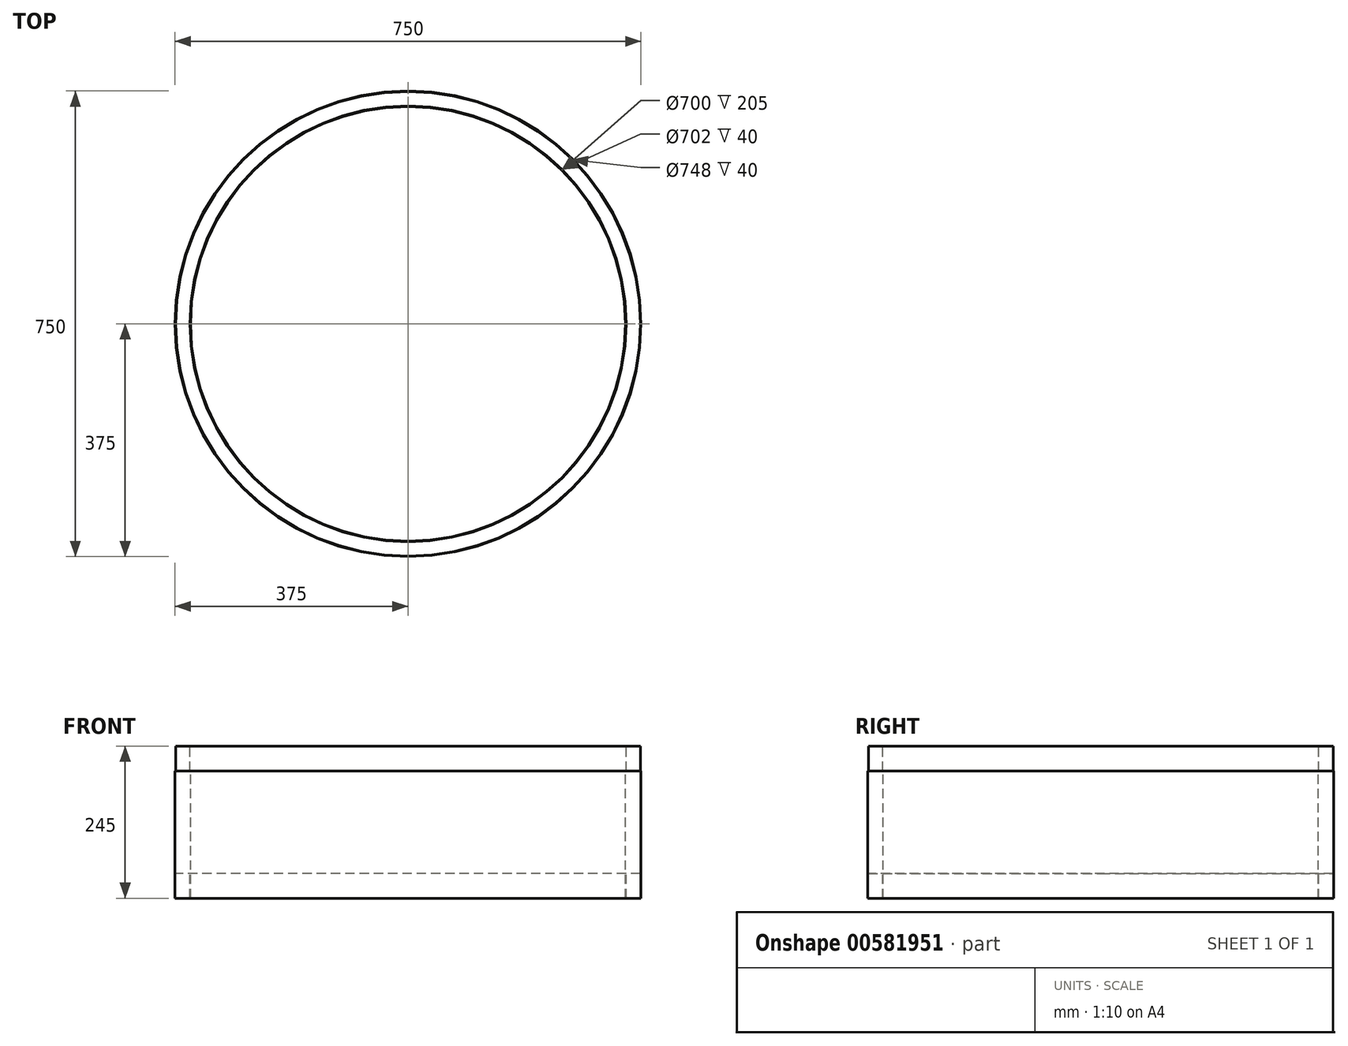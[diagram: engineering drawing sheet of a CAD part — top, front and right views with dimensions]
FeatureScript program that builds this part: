
annotation { "Feature Type Name" : "Feature", "Feature Type Description" : "" }
export const myFeature = defineFeature(function(context is Context, id is Id, definition is map)
    precondition{}
    {
        {
            var Q0;
            Q0=qCreatedBy(makeId("Front.planeOp"),FACE);
            var sketch = newSketch(context, id + "F0", { "sketchPlane" : qUnion([Q0])});
            skLineSegment(sketch, "E0", {"start": v(0, 345.75) * mm, "end": v(0, -558.03) * mm, "construction": true});
            skLineSegment(sketch, "E1", {"start": v(-350, -518.84) * mm, "end": v(-350, -313.84) * mm});
            skLineSegment(sketch, "E2", {"start": v(-350, -313.84) * mm, "end": v(-351, -313.84) * mm});
            skLineSegment(sketch, "E3", {"start": v(-351, -313.84) * mm, "end": v(-351, -273.84) * mm});
            skLineSegment(sketch, "E4", {"start": v(-351, -273.84) * mm, "end": v(-374, -273.84) * mm});
            skLineSegment(sketch, "E5", {"start": v(-374, -273.84) * mm, "end": v(-374, -313.84) * mm});
            skLineSegment(sketch, "E6", {"start": v(-374, -313.84) * mm, "end": v(-375, -313.84) * mm});
            skLineSegment(sketch, "E7", {"start": v(-375, -313.84) * mm, "end": v(-375, -518.84) * mm});
            skLineSegment(sketch, "E8", {"start": v(-375, -518.84) * mm, "end": v(-374, -518.84) * mm});
            skLineSegment(sketch, "E9", {"start": v(-374, -518.84) * mm, "end": v(-374, -478.84) * mm});
            skLineSegment(sketch, "E10", {"start": v(-374, -478.84) * mm, "end": v(-351, -478.84) * mm});
            skLineSegment(sketch, "E11", {"start": v(-351, -478.84) * mm, "end": v(-351, -518.84) * mm});
            skLineSegment(sketch, "E12", {"start": v(-351, -518.84) * mm, "end": v(-350, -518.84) * mm});
            skSolve(sketch);
        }
        {
            var Q0;
            Q0=qSketchRegion(id+"F0",true);
            var Q1;
            Q1=sQuery(id+"F0.wireOp",EDGE,"E0");
            revolve(context, id + "F1", {"entities" : qUnion([Q0]), "axis" : qUnion([Q1]), "revolveType" : RevolveType.FULL});
        }
    });
